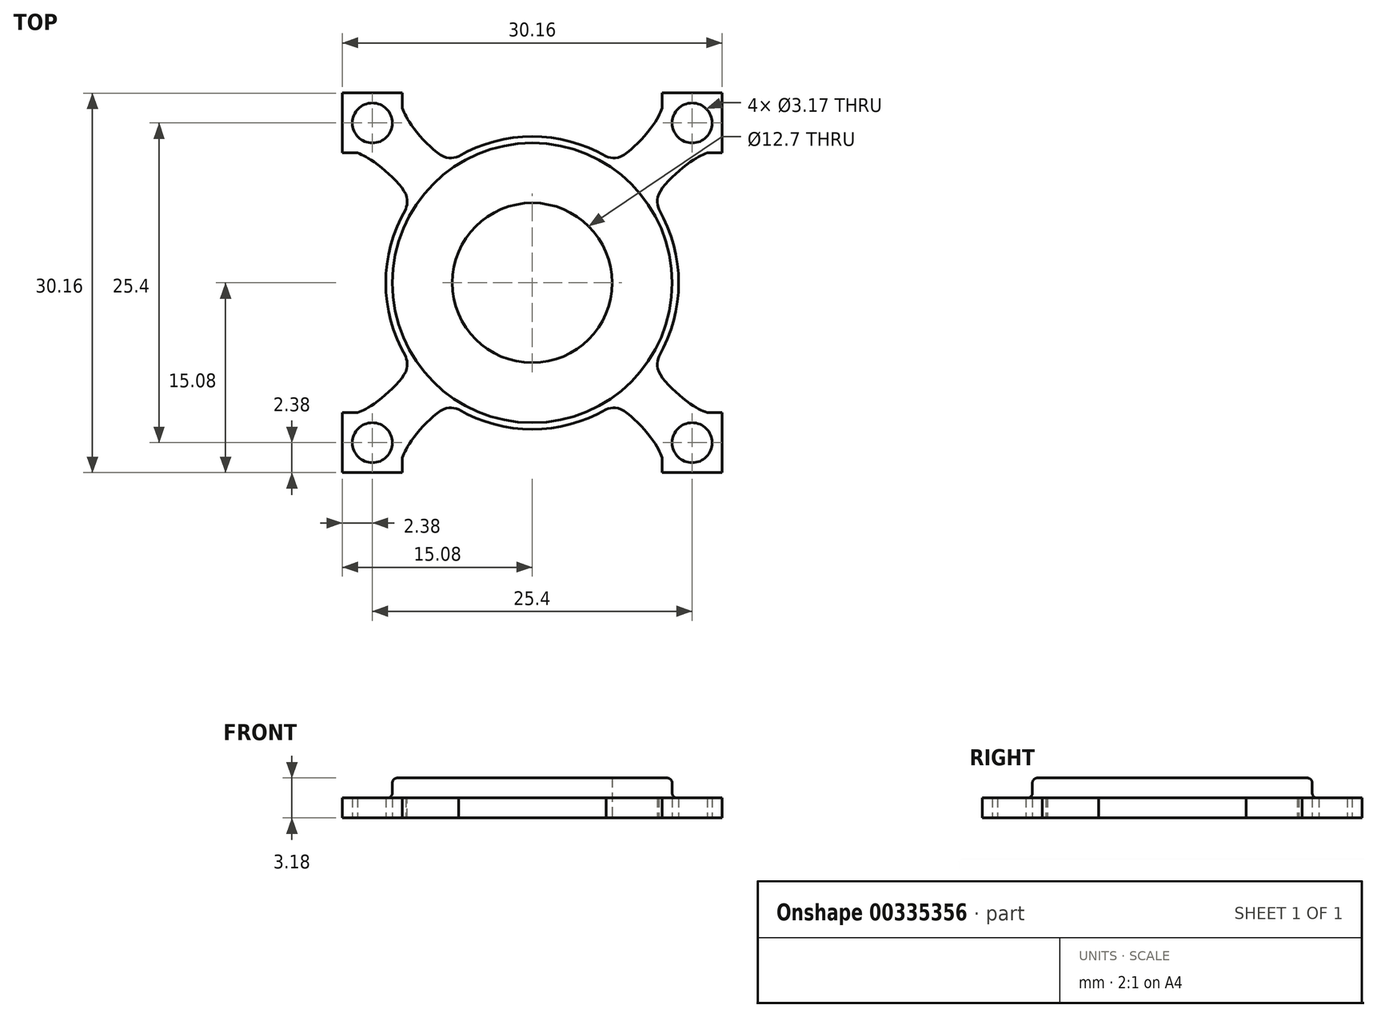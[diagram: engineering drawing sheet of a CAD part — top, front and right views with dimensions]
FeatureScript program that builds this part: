
annotation { "Feature Type Name" : "Feature", "Feature Type Description" : "" }
export const myFeature = defineFeature(function(context is Context, id is Id, definition is map)
    precondition{}
    {
        {
            var Q0;
            Q0=qCreatedBy(makeId("Top.planeOp"),FACE);
            var sketch = newSketch(context, id + "F0", { "sketchPlane" : qUnion([Q0])});
            skLineSegment(sketch, "E0.bottom", {"start": v(12.7, -12.7) * mm, "end": v(-12.7, -12.7) * mm, "construction": true});
            skLineSegment(sketch, "E0.top", {"start": v(12.7, 12.7) * mm, "end": v(-12.7, 12.7) * mm, "construction": true});
            skLineSegment(sketch, "E0.left", {"start": v(12.7, -12.7) * mm, "end": v(12.7, 12.7) * mm, "construction": true});
            skLineSegment(sketch, "E0.right", {"start": v(-12.7, -12.7) * mm, "end": v(-12.7, 12.7) * mm, "construction": true});
            skPoint(sketch, "E0.middle", {"position": v(0, 0) * mm});
            skCircle(sketch, "E1", {"center": v(0, 0) * mm, "radius": 11.63 * mm});
            skCircle(sketch, "E2", {"center": v(0, 0) * mm, "radius": 6.35 * mm});
            skCircle(sketch, "E3", {"center": v(-12.7, -12.7) * mm, "radius": 1.59 * mm});
            skLineSegment(sketch, "E4.bottom", {"start": v(-10.32, -15.08) * mm, "end": v(-15.08, -15.08) * mm});
            skLineSegment(sketch, "E4.top", {"start": v(-10.32, -10.32) * mm, "end": v(-15.08, -10.32) * mm});
            skLineSegment(sketch, "E4.left", {"start": v(-10.32, -15.08) * mm, "end": v(-10.32, -10.32) * mm});
            skLineSegment(sketch, "E4.right", {"start": v(-15.08, -15.08) * mm, "end": v(-15.08, -10.32) * mm});
            skPoint(sketch, "E5", {"position": v(-13.9, -10.32) * mm});
            skPoint(sketch, "E6", {"position": v(-10.32, -13.9) * mm});
            skLineSegment(sketch, "E7", {"start": v(0, 0) * mm, "end": v(-12.7, -12.7) * mm});
            skLineSegment(sketch, "E8.1.0", {"start": v(15.08, -15.08) * mm, "end": v(10.32, -15.08) * mm});
            skPoint(sketch, "E8.1.1", {"position": v(12.7, -12.7) * mm});
            skLineSegment(sketch, "E8.1.2", {"start": v(10.32, -10.32) * mm, "end": v(10.32, -15.08) * mm});
            skLineSegment(sketch, "E8.1.3", {"start": v(15.08, -10.32) * mm, "end": v(10.32, -10.32) * mm});
            skPoint(sketch, "E8.1.4", {"position": v(13.9, -10.32) * mm});
            skLineSegment(sketch, "E8.1.5", {"start": v(15.08, -10.32) * mm, "end": v(15.08, -15.08) * mm});
            skCircle(sketch, "E8.1.6", {"center": v(12.7, -12.7) * mm, "radius": 1.59 * mm});
            skPoint(sketch, "E8.1.7", {"position": v(10.32, -13.9) * mm});
            skLineSegment(sketch, "E8.2.0", {"start": v(15.08, 15.08) * mm, "end": v(15.08, 10.32) * mm});
            skPoint(sketch, "E8.2.1", {"position": v(12.7, 12.7) * mm});
            skLineSegment(sketch, "E8.2.2", {"start": v(10.32, 10.32) * mm, "end": v(15.08, 10.32) * mm});
            skLineSegment(sketch, "E8.2.3", {"start": v(10.32, 15.08) * mm, "end": v(10.32, 10.32) * mm});
            skPoint(sketch, "E8.2.4", {"position": v(10.32, 13.9) * mm});
            skLineSegment(sketch, "E8.2.5", {"start": v(10.32, 15.08) * mm, "end": v(15.08, 15.08) * mm});
            skCircle(sketch, "E8.2.6", {"center": v(12.7, 12.7) * mm, "radius": 1.59 * mm});
            skPoint(sketch, "E8.2.7", {"position": v(13.9, 10.32) * mm});
            skLineSegment(sketch, "E8.3.0", {"start": v(-15.08, 15.08) * mm, "end": v(-10.32, 15.08) * mm});
            skPoint(sketch, "E8.3.1", {"position": v(-12.7, 12.7) * mm});
            skLineSegment(sketch, "E8.3.2", {"start": v(-10.32, 10.32) * mm, "end": v(-10.32, 15.08) * mm});
            skLineSegment(sketch, "E8.3.3", {"start": v(-15.08, 10.32) * mm, "end": v(-10.32, 10.32) * mm});
            skPoint(sketch, "E8.3.4", {"position": v(-13.9, 10.32) * mm});
            skLineSegment(sketch, "E8.3.5", {"start": v(-15.08, 10.32) * mm, "end": v(-15.08, 15.08) * mm});
            skCircle(sketch, "E8.3.6", {"center": v(-12.7, 12.7) * mm, "radius": 1.59 * mm});
            skPoint(sketch, "E8.3.7", {"position": v(-10.32, 13.9) * mm});
            skLineSegment(sketch, "E9", {"start": v(-9.7, -12.7) * mm, "end": v(-7.05, -10.05) * mm, "construction": true});
            skLineSegment(sketch, "E10.MirrorCS", {"start": v(-12.7, -9.7) * mm, "end": v(-10.05, -7.05) * mm, "construction": true});
            skLineSegment(sketch, "E11.1.0", {"start": v(9.7, -12.7) * mm, "end": v(7.05, -10.05) * mm, "construction": true});
            skLineSegment(sketch, "E11.1.1", {"start": v(12.7, -9.7) * mm, "end": v(10.05, -7.05) * mm, "construction": true});
            skLineSegment(sketch, "E11.2.0", {"start": v(12.7, 9.7) * mm, "end": v(10.05, 7.05) * mm, "construction": true});
            skLineSegment(sketch, "E11.2.1", {"start": v(9.7, 12.7) * mm, "end": v(7.05, 10.05) * mm, "construction": true});
            skLineSegment(sketch, "E11.3.0", {"start": v(-9.7, 12.7) * mm, "end": v(-7.05, 10.05) * mm, "construction": true});
            skLineSegment(sketch, "E11.3.1", {"start": v(-12.7, 9.7) * mm, "end": v(-10.05, 7.05) * mm, "construction": true});
            skFitSpline(sketch, "E12", {"points": [v(10.32, -13.9) * mm, v(9.7, -12.7) * mm, v(7.05, -10.05) * mm, v(5.86, -10.05) * mm], "startDerivative": vector(-1.42, 3.63) * mm, "endDerivative": vector(-4.13, -1.24) * mm});
            skLineSegment(sketch, "E13", {"start": v(12.7, -12.7) * mm, "end": v(0, 0) * mm, "construction": true});
            skFitSpline(sketch, "E14.MirrorCS", {"points": [v(13.9, -10.32) * mm, v(12.7, -9.7) * mm, v(10.05, -7.05) * mm, v(10.05, -5.86) * mm], "startDerivative": vector(-3.63, 1.42) * mm, "endDerivative": vector(1.24, 4.13) * mm});
            skFitSpline(sketch, "E15", {"points": [v(-13.9, 10.32) * mm, v(-12.7, 9.7) * mm, v(-10.05, 7.05) * mm, v(-10.05, 5.86) * mm], "startDerivative": vector(3.63, -1.42) * mm, "endDerivative": vector(-1.24, -4.13) * mm});
            skFitSpline(sketch, "E16", {"points": [v(-10.32, 13.9) * mm, v(-9.7, 12.7) * mm, v(-7.05, 10.05) * mm, v(-5.86, 10.05) * mm], "startDerivative": vector(1.42, -3.63) * mm, "endDerivative": vector(4.13, 1.24) * mm});
            skFitSpline(sketch, "E17", {"points": [v(10.32, 13.9) * mm, v(9.7, 12.7) * mm, v(7.05, 10.05) * mm, v(5.86, 10.05) * mm], "startDerivative": vector(-1.42, -3.63) * mm, "endDerivative": vector(-4.13, 1.24) * mm});
            skFitSpline(sketch, "E18", {"points": [v(13.9, 10.32) * mm, v(12.7, 9.7) * mm, v(10.05, 7.05) * mm, v(10.05, 5.86) * mm], "startDerivative": vector(-3.63, -1.42) * mm, "endDerivative": vector(1.24, -4.13) * mm});
            skFitSpline(sketch, "E19", {"points": [v(-10.32, -13.9) * mm, v(-9.7, -12.7) * mm, v(-7.05, -10.05) * mm, v(-5.86, -10.05) * mm], "startDerivative": vector(1.42, 3.63) * mm, "endDerivative": vector(4.13, -1.24) * mm});
            skFitSpline(sketch, "E20", {"points": [v(-13.9, -10.32) * mm, v(-12.7, -9.7) * mm, v(-10.05, -7.05) * mm, v(-10.05, -5.86) * mm], "startDerivative": vector(3.63, 1.42) * mm, "endDerivative": vector(-1.24, 4.13) * mm});
            skCircle(sketch, "E21", {"center": v(0, 0) * mm, "radius": 11.11 * mm});
            skSolve(sketch);
        }
        {
            var Q0;
            Q0=makeQuery(id+"F0.imprint","IMPRINT",FACE,{"disambiguationData":[TD([[makeQuery(id+"F0.imprint","IMPRINT",EDGE,{"derivedFrom":sQuery(id+"F0.wireOp",EDGE,"E2")}),-1.0]])]});
            extrude(context, id + "F1", {"entities" : qUnion([Q0]), "depth" : 3.17 * mm});
        }
        {
            var Q0;
            Q0=makeQuery(id+"F0.imprint","IMPRINT",FACE,{"disambiguationData":[TD([[makeQuery(id+"F0.imprint","IMPRINT",EDGE,{"derivedFrom":sQuery(id+"F0.wireOp",EDGE,"E21")}),-1.0]])]});
            var Q1;
            {var subQ0=sQuery(id+"F0.wireOp",EDGE,"E15");Q1=makeQuery(id+"F0.imprint","IMPRINT",FACE,{"disambiguationData":[TD([[makeQuery(id+"F0.imprint","IMPRINT",EDGE,{"derivedFrom":subQ0}),1.0]])]});}
            var Q2;
            {var subQ4=sQuery(id+"F0.wireOp",EDGE,"E8.3.0");Q2=makeQuery(id+"F0.imprint","IMPRINT",FACE,{"disambiguationData":[TD([[makeQuery(id+"F0.imprint","IMPRINT",EDGE,{"derivedFrom":subQ4}),-1.0]])]});}
            var Q3;
            {var subQ0=sQuery(id+"F0.wireOp",EDGE,"E17");Q3=makeQuery(id+"F0.imprint","IMPRINT",FACE,{"disambiguationData":[TD([[makeQuery(id+"F0.imprint","IMPRINT",EDGE,{"derivedFrom":subQ0}),1.0]])]});}
            var Q4;
            {var subQ4=sQuery(id+"F0.wireOp",EDGE,"E8.2.0");Q4=makeQuery(id+"F0.imprint","IMPRINT",FACE,{"disambiguationData":[TD([[makeQuery(id+"F0.imprint","IMPRINT",EDGE,{"derivedFrom":subQ4}),-1.0]])]});}
            var Q5;
            {var subQ0=sQuery(id+"F0.wireOp",EDGE,"E12");Q5=makeQuery(id+"F0.imprint","IMPRINT",FACE,{"disambiguationData":[TD([[makeQuery(id+"F0.imprint","IMPRINT",EDGE,{"derivedFrom":subQ0}),-1.0]])]});}
            var Q6;
            {var subQ4=sQuery(id+"F0.wireOp",EDGE,"E8.1.0");Q6=makeQuery(id+"F0.imprint","IMPRINT",FACE,{"disambiguationData":[TD([[makeQuery(id+"F0.imprint","IMPRINT",EDGE,{"derivedFrom":subQ4}),-1.0]])]});}
            var Q7;
            {var subQ0=sQuery(id+"F0.wireOp",EDGE,"E19");Q7=makeQuery(id+"F0.imprint","IMPRINT",FACE,{"disambiguationData":[TD([[makeQuery(id+"F0.imprint","IMPRINT",EDGE,{"derivedFrom":subQ0}),1.0]])]});}
            var Q8;
            {var subQ0=sQuery(id+"F0.wireOp",EDGE,"E20");Q8=makeQuery(id+"F0.imprint","IMPRINT",FACE,{"disambiguationData":[TD([[makeQuery(id+"F0.imprint","IMPRINT",EDGE,{"derivedFrom":subQ0}),-1.0]])]});}
            var Q9;
            Q9=makeQuery(id+"F0.imprint","IMPRINT",FACE,{"disambiguationData":[TD([[makeQuery(id+"F0.imprint","IMPRINT",EDGE,{"derivedFrom":sQuery(id+"F0.wireOp",EDGE,"E3")}),-1.0]])]});
            extrude(context, id + "F2", {"entities" : qUnion([Q0, Q1, Q2, Q3, Q4, Q5, Q6, Q7, Q8, Q9]), "operationType" : NewBodyOperationType.ADD, "depth" : 1.59 * mm});
        }
        {
            var Q0;
            Q0=makeQuery(id+"F1.opExtrude","SWEPT_FACE",FACE,{"disambiguationData":[OSD([sQuery(id+"F0.wireOp",EDGE,"E21")])]});
            fillet(context, id + "F3", {"entities" : qUnion([Q0]), "radius" : 0.4 * mm, "tangentPropagation" : true, "allowEdgeOverflow" : false});
        }
    });
